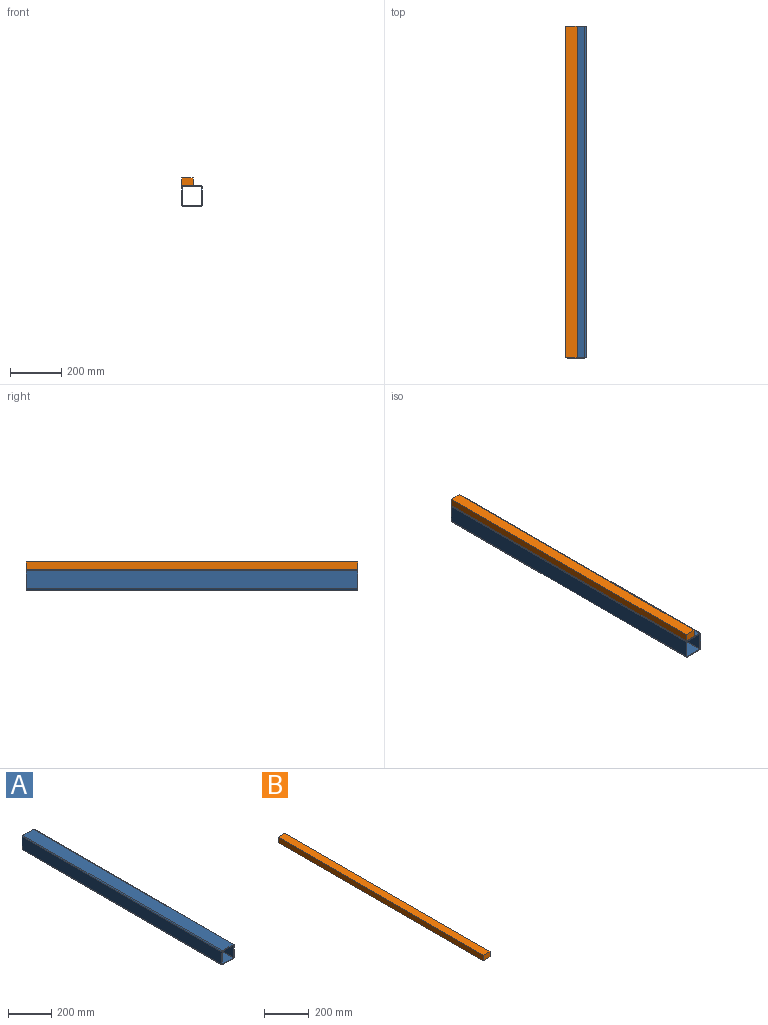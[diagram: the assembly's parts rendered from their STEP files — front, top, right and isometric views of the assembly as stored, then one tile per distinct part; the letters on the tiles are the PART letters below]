
ASSEMBLY  parts=2 mates=1
PART A: 18 faces, bbox 80x1300x80 mm
  f0: cylinder r=1mm len=1300mm, axis (0,-1,0), area 2042mm2, adj f1,f15,f16,f17
  f1: plane 1300x70mm, normal (-1,0,0), area 91000mm2, adj f0,f2,f16,f17
  f2: cylinder r=1mm len=1300mm, axis (0,-1,0), area 2042mm2, adj f1,f3,f16,f17
  f3: plane 1300x70mm, normal (0,0,1), area 91000mm2, adj f2,f4,f16,f17
  f4: cylinder r=1mm len=1300mm, axis (0,-1,0), area 2042mm2, adj f3,f5,f16,f17
  f5: plane 1300x70mm, normal (1,0,0), area 91000mm2, adj f4,f6,f16,f17
  f6: cylinder r=1mm len=1300mm, axis (0,-1,0), area 2042mm2, adj f5,f15,f16,f17
  f7: plane 1300x70mm, normal (0,0,-1), area 91000mm2, adj f8,f14,f16,f17
  f8: cylinder r=5mm len=1300mm, axis (0,-1,0), area 10210.2mm2, adj f7,f9,f16,f17
  f9: plane 1300x70mm, normal (1,0,0), area 91000mm2, adj f8,f10,f16,f17
  f10: cylinder r=5mm len=1300mm, axis (0,-1,0), area 10210.2mm2, adj f9,f11,f16,f17
  f11: plane 1300x70mm, normal (0,0,1), area 91000mm2, adj f10,f12,f16,f17
  f12: cylinder r=5mm len=1300mm, axis (0,-1,0), area 10210.2mm2, adj f11,f13,f16,f17
  f13: plane 1300x70mm, normal (-1,0,0), area 91000mm2, adj f12,f14,f16,f17
  f14: cylinder r=5mm len=1300mm, axis (0,-1,0), area 10210.2mm2, adj f7,f13,f16,f17
  f15: plane 1300x70mm, normal (0,0,-1), area 91000mm2, adj f0,f6,f16,f17
  f16: plane 80x80mm, normal (0,1,0), area 1195.4mm2, adj f0,f1,f2,f3,f4,f5,f6,f7
  f17: plane 80x80mm, normal (0,-1,0), area 1195.4mm2, adj f0,f1,f2,f3,f4,f5,f6,f7
PART B: 6 faces, bbox 44x1300x30 mm
  f0: plane 1300x30mm, normal (1,0,0), area 39000mm2, adj f1,f3,f4,f5
  f1: plane 1300x44mm, normal (0,0,1), area 57200mm2, adj f0,f2,f4,f5
  f2: plane 1300x30mm, normal (-1,0,0), area 39000mm2, adj f1,f3,f4,f5
  f3: plane 1300x44mm, normal (0,0,-1), area 57200mm2, adj f0,f2,f4,f5
  f4: plane 44x30mm, normal (0,1,0), area 1320mm2, adj f0,f1,f2,f3
  f5: plane 44x30mm, normal (0,-1,0), area 1320mm2, adj f0,f1,f2,f3
PLACE A t=(43.62,-364.41,390.61)mm
PLACE B t=(25.62,-364.41,445.61)mm
MATE fastened B.f5 <-> A.f17  axis (0,-1,0) through (25.62,-364.41,430.61)mm
